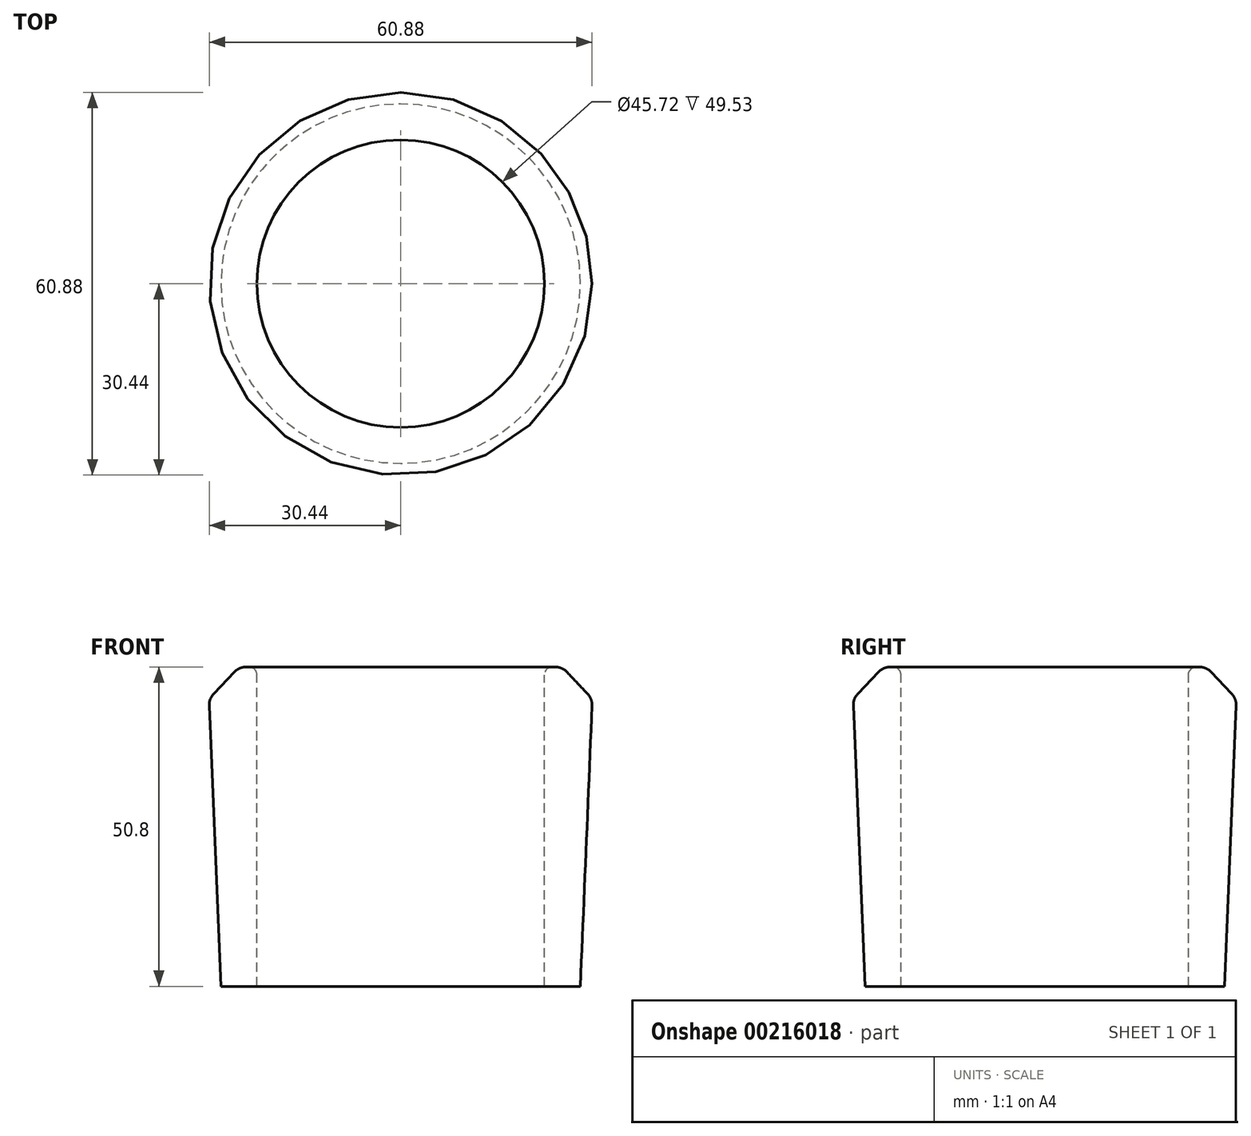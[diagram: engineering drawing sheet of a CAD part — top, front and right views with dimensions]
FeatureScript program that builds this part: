
annotation { "Feature Type Name" : "Feature", "Feature Type Description" : "" }
export const myFeature = defineFeature(function(context is Context, id is Id, definition is map)
    precondition{}
    {
        {
            var Q0;
            Q0=qCreatedBy(makeId("Front.planeOp"),FACE);
            var sketch = newSketch(context, id + "F0", { "sketchPlane" : qUnion([Q0])});
            skLineSegment(sketch, "E0", {"start": v(-28.58, 0) * mm, "end": v(-30.44, 44.64) * mm});
            skLineSegment(sketch, "E1", {"start": v(-29.74, 46.5) * mm, "end": v(-26.4, 50) * mm});
            skLineSegment(sketch, "E2", {"start": v(-25.65, 50.8) * mm, "end": v(-25.65, 50.8) * mm});
            skLineSegment(sketch, "E3", {"start": v(-28.58, 0) * mm, "end": v(-22.86, 0) * mm});
            skLineSegment(sketch, "E4", {"start": v(-24.56, 50.8) * mm, "end": v(-24.13, 50.8) * mm});
            skLineSegment(sketch, "E5", {"start": v(-22.86, 49.53) * mm, "end": v(-22.86, 12.7) * mm});
            skLineSegment(sketch, "E6", {"start": v(-22.86, 50.8) * mm, "end": v(0, 50.8) * mm, "construction": true});
            skLineSegment(sketch, "E7", {"start": v(0, 50.8) * mm, "end": v(0, 0) * mm, "construction": true});
            skPoint(sketch, "E8.visualSharp", {"position": v(-25.65, 50.8) * mm});
            skArc(sketch, "E8.filletArc", {"start": v(-24.56, 50.8) * mm, "mid": v(-25.57, 50.6) * mm, "end": v(-26.4, 50) * mm});
            skPoint(sketch, "E9.visualSharp", {"position": v(-30.48, 45.72) * mm});
            skArc(sketch, "E9.filletArc", {"start": v(-29.74, 46.5) * mm, "mid": v(-30.28, 45.64) * mm, "end": v(-30.44, 44.64) * mm});
            skPoint(sketch, "E10.visualSharp", {"position": v(-22.86, 50.8) * mm});
            skArc(sketch, "E10.filletArc", {"start": v(-22.86, 49.53) * mm, "mid": v(-23.23, 50.43) * mm, "end": v(-24.13, 50.8) * mm});
            skLineSegment(sketch, "E11", {"start": v(-22.86, 0) * mm, "end": v(-22.86, 12.7) * mm});
            skLineSegment(sketch, "E12", {"start": v(-22.86, 0) * mm, "end": v(0, 0) * mm, "construction": true});
            skSolve(sketch);
        }
        {
            var Q0;
            Q0=makeQuery(id+"F0.imprint","IMPRINT",FACE,{"disambiguationData":[TD([[makeQuery(id+"F0.imprint","IMPRINT",EDGE,{"derivedFrom":sQuery(id+"F0.wireOp",EDGE,"E0")}),-1.0]])]});
            var Q1;
            Q1=sQuery(id+"F0.wireOp",EDGE,"E7");
            revolve(context, id + "F1", {"entities" : qUnion([Q0]), "axis" : qUnion([Q1]), "revolveType" : RevolveType.FULL});
        }
    });
